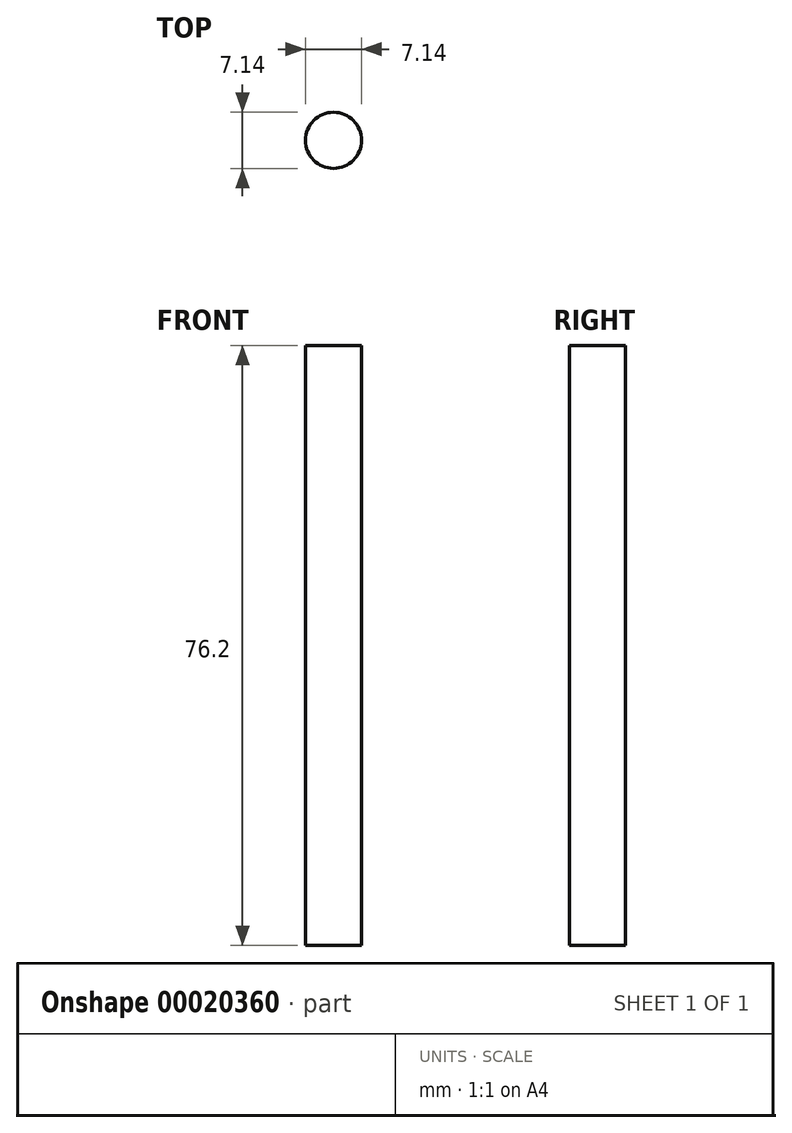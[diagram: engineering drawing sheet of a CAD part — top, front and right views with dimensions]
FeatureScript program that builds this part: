
annotation { "Feature Type Name" : "Feature", "Feature Type Description" : "" }
export const myFeature = defineFeature(function(context is Context, id is Id, definition is map)
    precondition{}
    {
        {
            var Q0;
            Q0=qCreatedBy(makeId("Front.planeOp"),FACE);
            var sketch = newSketch(context, id + "F0", { "sketchPlane" : qUnion([Q0])});
            skLineSegment(sketch, "E0.bottom", {"start": v(-47.9, 27.5) * mm, "end": v(47.36, 27.5) * mm});
            skLineSegment(sketch, "E0.top", {"start": v(-47.9, -48.7) * mm, "end": v(47.36, -48.7) * mm});
            skLineSegment(sketch, "E0.left", {"start": v(-47.9, 27.5) * mm, "end": v(-47.9, -48.7) * mm});
            skLineSegment(sketch, "E0.right", {"start": v(47.36, 27.5) * mm, "end": v(47.36, -48.7) * mm});
            skCircle(sketch, "E1", {"center": v(-0.4, -10.6) * mm, "radius": 23.75 * mm});
            skSolve(sketch);
        }
        {
            var Q0;
            {var subQ8=sQuery(id+"F0.wireOp",EDGE,"E0.left");Q0=makeQuery(id+"F0.imprint","IMPRINT",FACE,{"disambiguationData":[TD([[makeQuery(id+"F0.imprint","IMPRINT",EDGE,{"derivedFrom":subQ8}),1.0]])]});}
            var Q1;
            {var subQ8=sQuery(id+"F0.wireOp",EDGE,"E0.right");Q1=makeQuery(id+"F0.imprint","IMPRINT",FACE,{"disambiguationData":[TD([[makeQuery(id+"F0.imprint","IMPRINT",EDGE,{"derivedFrom":subQ8}),-1.0]])]});}
            extrude(context, id + "F1", {"entities" : qUnion([Q0, Q1]), "depth" : 25.4 * mm});
        }
        {
            var Q0;
            Q0=makeQuery(id+"F1.opExtrude","SWEPT_FACE",FACE,{"disambiguationData":[OSD([sQuery(id+"F0.wireOp",EDGE,"E0.bottom")])]});
            var sketch = newSketch(context, id + "F2", { "sketchPlane" : qUnion([Q0])});
            skCircle(sketch, "E2", {"center": v(-38.37, -12.7) * mm, "radius": 3.57 * mm});
            skCircle(sketch, "E3.MirrorC", {"center": v(38.37, -12.7) * mm, "radius": 3.57 * mm});
            skSolve(sketch);
        }
        {
            var Q0;
            Q0=makeQuery(id+"F2.imprint","IMPRINT",FACE,{"disambiguationData":[TD([[makeQuery(id+"F2.imprint","IMPRINT",EDGE,{"derivedFrom":sQuery(id+"F2.wireOp",EDGE,"E3.MirrorC")}),-1.0]])]});
            var Q1;
            Q1=makeQuery(id+"F2.imprint","IMPRINT",FACE,{"disambiguationData":[TD([[makeQuery(id+"F2.imprint","IMPRINT",EDGE,{"derivedFrom":sQuery(id+"F2.wireOp",EDGE,"E2")}),1.0]])]});
            extrude(context, id + "F3", {"entities" : qUnion([Q0, Q1]), "operationType" : NewBodyOperationType.REMOVE, "oppositeDirection" : true, "depth" : 76.2 * mm});
        }
    });
